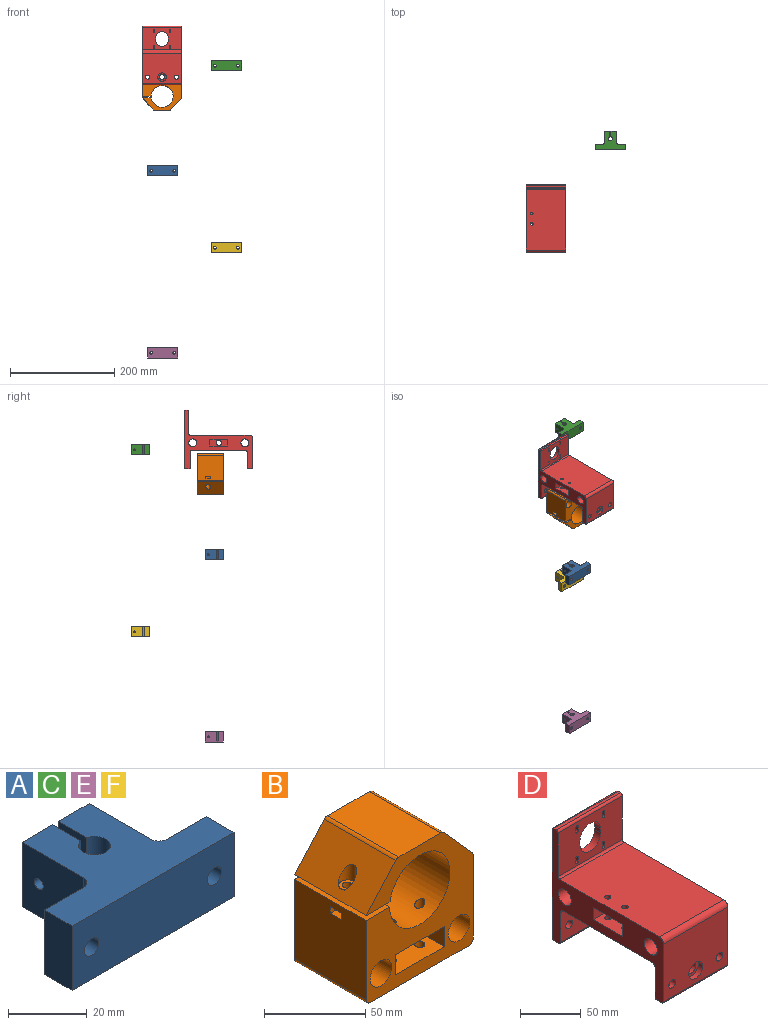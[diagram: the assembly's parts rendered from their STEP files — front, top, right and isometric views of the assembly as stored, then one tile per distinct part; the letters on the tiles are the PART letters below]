
ASSEMBLY  parts=6 mates=3
PART A: 27 faces, bbox 58.1x35x20 mm
  f0: plane 22x20mm, normal (1,0,0), area 413.8mm2, adj f5,f6,f15,f16,f18,f19,f20,f21
  f1: cylinder r=1.6mm len=8.05mm, axis (-1,0,0), area 80.9mm2, adj f7,f24
  f2: plane 58.1x20mm, normal (0,-1,0), area 1119.5mm2, adj f3,f14,f15,f16,f25,f26
  f3: plane 20x10mm, normal (1,0,0), area 200mm2, adj f2,f4,f15,f16
  f4: plane 20x14mm, normal (0,1,0), area 258.8mm2, adj f3,f5,f15,f16,f26
  f5: cylinder r=3mm len=20mm, axis (0,0,-1), area 94.2mm2, adj f0,f4,f15,f16
  f6: plane 20x11.05mm, normal (0,1,0), area 221mm2, adj f0,f7,f15,f16
  f7: plane 20x10.08mm, normal (-1,0,0), area 193.5mm2, adj f1,f6,f8,f15,f16
  f8: cylinder r=4.05mm len=20mm, axis (0,0,-1), area 468.5mm2, adj f7,f9,f15,f16
  f9: plane 20x10.08mm, normal (1,0,0), area 193.5mm2, adj f8,f10,f15,f16,f17
  f10: plane 20x11.05mm, normal (0,1,0), area 221mm2, adj f9,f11,f15,f16
  f11: plane 22x20mm, normal (-1,0,0), area 432mm2, adj f10,f12,f15,f16,f17
  f12: cylinder r=3mm len=20mm, axis (0,0,-1), area 94.2mm2, adj f11,f13,f15,f16
  f13: plane 20x14mm, normal (0,1,0), area 258.8mm2, adj f12,f14,f15,f16,f25
  f14: plane 20x10mm, normal (-1,0,0), area 200mm2, adj f2,f13,f15,f16
  f15: plane 58.1x35mm, normal (0,0,1), area 1115.8mm2, adj f0,f2,f3,f4,f5,f6,f7,f8
  f16: plane 58.1x35mm, normal (0,0,-1), area 1115.8mm2, adj f0,f2,f3,f4,f5,f6,f7,f8
  f17: cylinder r=1.6mm len=11.05mm, axis (-1,0,0), area 111.1mm2, adj f9,f11
  f18: plane 3.18x3mm, normal (0,1,0), area 9.5mm2, adj f0,f19,f23,f24
  f19: plane 3x2.75mm, normal (0,0.5,0.87), area 9.5mm2, adj f0,f18,f20,f24
  f20: plane 3x2.75mm, normal (0,-0.5,0.87), area 9.5mm2, adj f0,f19,f21,f24
  f21: plane 3.18x3mm, normal (0,-1,0), area 9.5mm2, adj f0,f20,f22,f24
  f22: plane 3x2.75mm, normal (0,-0.5,-0.87), area 9.5mm2, adj f0,f21,f23,f24
  f23: plane 3x2.75mm, normal (0,0.5,-0.87), area 9.5mm2, adj f0,f18,f22,f24
  f24: plane 6.35x5.5mm, normal (1,0,0), area 18.2mm2, adj f1,f18,f19,f20,f21,f22,f23
  f25: cylinder r=2.6mm len=10mm, axis (0,-1,0), area 163.4mm2, adj f2,f13
  f26: cylinder r=2.6mm len=10mm, axis (0,-1,0), area 163.4mm2, adj f2,f4
PART B: 40 faces, bbox 75x50x78.1 mm
  f0: plane 50x48mm, normal (-1,0,0), area 2367.6mm2, adj f2,f4,f9,f27,f33,f34,f35,f36
  f1: cylinder r=2.55mm len=5.1mm, axis (0,0,1), area 64.1mm2, adj f9,f33
  f2: plane 78.05x75mm, normal (0,-1,0), area 3115mm2, adj f0,f5,f6,f7,f8,f9,f10,f11
  f3: cylinder r=4.5mm len=29mm, axis (0,1,0), area 820mm2, adj f4,f22
  f4: plane 78.05x75mm, normal (0,1,0), area 3468.6mm2, adj f0,f3,f5,f6,f7,f8,f9,f10
  f5: plane 50x49.86mm, normal (1,0,0), area 2492.8mm2, adj f2,f4,f17,f28
  f6: plane 69x50mm, normal (0,0,-1), area 3409.1mm2, adj f2,f4,f23,f24,f27,f28
  f7: cylinder r=7.55mm len=50mm, axis (0,1,0), area 2371.9mm2, adj f2,f4
  f8: cylinder r=7.55mm len=50mm, axis (0,1,0), area 2371.9mm2, adj f2,f4
  f9: plane 50x16.51mm, normal (0,0,1), area 805mm2, adj f0,f1,f2,f4,f10
  f10: cylinder r=21.05mm len=50mm, axis (0,1,0), area 6416mm2, adj f2,f4,f9,f11,f25,f26
  f11: plane 50x16.72mm, normal (0,0,-1), area 815.7mm2, adj f2,f4,f10,f12,f31
  f12: plane 50x23.05mm, normal (-0.74,0,0.67), area 1452.6mm2, adj f2,f4,f11,f13,f29,f30
  f13: cylinder r=3mm len=50mm, axis (0,1,0), area 126mm2, adj f2,f4,f12,f14
  f14: plane 50x29.32mm, normal (0,0,1), area 1465.8mm2, adj f2,f4,f13,f15
  f15: cylinder r=3mm len=50mm, axis (0,1,0), area 126.4mm2, adj f2,f4,f14,f16
  f16: plane 50x22.19mm, normal (0.75,0,0.67), area 1486.7mm2, adj f2,f4,f15,f17
  f17: cylinder r=3mm len=50mm, axis (0,1,0), area 109.2mm2, adj f2,f4,f5,f16
  f18: plane 34.2x21mm, normal (0,0,-1), area 677.3mm2, adj f2,f19,f21,f22,f25,f26
  f19: plane 21x12.2mm, normal (1,0,0), area 256.2mm2, adj f2,f18,f20,f22
  f20: plane 34.2x21mm, normal (0,0,1), area 677.3mm2, adj f2,f19,f21,f22,f23,f24
  f21: plane 21x12.2mm, normal (-1,0,0), area 256.2mm2, adj f2,f18,f20,f22
  f22: plane 34.2x12.2mm, normal (0,-1,0), area 353.6mm2, adj f3,f18,f19,f20,f21
  f23: cylinder r=2.55mm len=7.9mm, axis (0,0,-1), area 126.6mm2, adj f6,f20
  f24: cylinder r=2.55mm len=7.9mm, axis (0,0,-1), area 126.6mm2, adj f6,f20
  f25: cylinder r=2.55mm len=14mm, axis (0,0,-1), area 200.1mm2, adj f10,f18
  f26: cylinder r=2.55mm len=14mm, axis (0,0,-1), area 200.1mm2, adj f10,f18
  f27: cylinder r=3mm len=50mm, axis (0,-1,0), area 235.6mm2, adj f0,f2,f4,f6
  f28: cylinder r=3mm len=50mm, axis (0,1,0), area 235.6mm2, adj f2,f4,f5,f6
  f29: cylinder r=4.5mm len=10.01mm, axis (0,0,-1), area 139.4mm2, adj f12,f32
  f30: cylinder r=4.5mm len=1.75mm, axis (0,0,-1), area 0.1mm2, adj f12,f32
  f31: cylinder r=2.55mm len=5.1mm, axis (0,0,-1), area 64.1mm2, adj f11,f32
  f32: plane 9x9mm, normal (0,0,1), area 43.2mm2, adj f29,f30,f31
  f33: plane 14.3x8.1mm, normal (0,0,-1), area 95.4mm2, adj f0,f1,f35,f36,f37
  f34: plane 14.3x8.1mm, normal (0,0,1), area 95.4mm2, adj f0,f35,f36,f37,f39
  f35: plane 14.3x4mm, normal (0,-1,0), area 57.2mm2, adj f0,f33,f34,f37
  f36: plane 14.3x4mm, normal (0,1,0), area 57.2mm2, adj f0,f33,f34,f37
  f37: plane 8.1x4mm, normal (-1,0,0), area 32.4mm2, adj f33,f34,f35,f36
  f38: plane 5.1x5.1mm, normal (0,0,1), area 20.4mm2, adj f39
  f39: cylinder r=2.55mm len=5.1mm, axis (0,0,1), area 64.1mm2, adj f34,f38
PART C: same geometry as A
PART D: 66 faces, bbox 75x130x113 mm
  f0: cylinder r=8.1mm len=16.2mm, axis (0,1,0), area 254.5mm2, adj f8,f65
  f1: cylinder r=8.1mm len=16.2mm, axis (0,1,0), area 254.5mm2, adj f2,f63
  f2: plane 109x75mm, normal (0,1,0), area 7242.7mm2, adj f1,f5,f9,f20,f21,f26,f40,f41
  f3: plane 75x44mm, normal (0,-1,0), area 2671.8mm2, adj f5,f9,f39,f41,f42,f43,f44,f45
  f4: plane 116x75mm, normal (0,0,1), area 8659.1mm2, adj f5,f9,f24,f34,f35,f61
  f5: plane 130x113mm, normal (-1,0,0), area 4154.8mm2, adj f2,f3,f4,f7,f8,f10,f11,f12
  f6: cylinder r=5mm len=54mm, axis (-1,0,0), area 1696.5mm2, adj f9,f33
  f7: plane 104x75mm, normal (0,0,-1), area 7759.1mm2, adj f5,f9,f16,f17,f36,f37
  f8: plane 75x58mm, normal (0,-1,0), area 4045.8mm2, adj f0,f5,f9,f18,f19,f24,f27
  f9: plane 130x113mm, normal (1,0,0), area 4493.5mm2, adj f2,f3,f4,f6,f7,f8,f10,f11
  f10: cylinder r=7.55mm len=75mm, axis (-1,0,0), area 3557.9mm2, adj f5,f9
  f11: cylinder r=7.55mm len=75mm, axis (-1,0,0), area 3557.9mm2, adj f5,f9
  f12: plane 75x30mm, normal (0,-1,0), area 2070.3mm2, adj f5,f9,f16,f20,f21,f25,f62
  f13: plane 75x6mm, normal (0,0,-1), area 450mm2, adj f5,f9,f25,f26
  f14: plane 75x30mm, normal (0,1,0), area 2070.3mm2, adj f5,f9,f17,f18,f19,f28,f64
  f15: plane 75x6mm, normal (0,0,-1), area 443.7mm2, adj f5,f9,f22,f23,f27,f28
  f16: cylinder r=3mm len=75mm, axis (1,0,0), area 353.4mm2, adj f5,f7,f9,f12
  f17: cylinder r=3mm len=75mm, axis (-1,0,0), area 353.4mm2, adj f5,f7,f9,f14
  f18: cylinder r=3.95mm len=10mm, axis (0,1,0), area 245mm2, adj f8,f14,f23
  f19: cylinder r=3.95mm len=10mm, axis (0,1,0), area 245mm2, adj f8,f14,f22
  f20: cylinder r=3.95mm len=10mm, axis (0,1,0), area 248.2mm2, adj f2,f12
  f21: cylinder r=3.95mm len=10mm, axis (0,1,0), area 248.2mm2, adj f2,f12
  f22: cylinder r=1mm len=11.18mm, axis (0,0,-1), area 69.8mm2, adj f15,f19
  f23: cylinder r=1mm len=11.18mm, axis (0,0,-1), area 69.8mm2, adj f15,f18
  f24: cylinder r=5mm len=75mm, axis (-1,0,0), area 589mm2, adj f4,f5,f8,f9
  f25: cylinder r=2mm len=75mm, axis (1,0,0), area 235.6mm2, adj f5,f9,f12,f13
  f26: cylinder r=2mm len=75mm, axis (1,0,0), area 235.6mm2, adj f2,f5,f9,f13
  f27: cylinder r=2mm len=75mm, axis (-1,0,0), area 235.6mm2, adj f5,f8,f9,f15
  f28: cylinder r=2mm len=75mm, axis (-1,0,0), area 235.6mm2, adj f5,f9,f14,f15
  f29: plane 21x12.2mm, normal (0,-1,0), area 256.2mm2, adj f5,f30,f32,f33
  f30: plane 34.2x21mm, normal (0,0,1), area 677.3mm2, adj f5,f29,f31,f33,f36,f37
  f31: plane 21x12.2mm, normal (0,1,0), area 256.2mm2, adj f5,f30,f32,f33
  f32: plane 34.2x21mm, normal (0,0,-1), area 677.3mm2, adj f5,f29,f31,f33,f34,f35
  f33: plane 34.2x12.2mm, normal (-1,0,0), area 338.7mm2, adj f6,f29,f30,f31,f32
  f34: cylinder r=2.55mm len=8.9mm, axis (0,0,1), area 142.6mm2, adj f4,f32
  f35: cylinder r=2.55mm len=8.9mm, axis (0,0,1), area 142.6mm2, adj f4,f32
  f36: cylinder r=2.55mm len=8.9mm, axis (0,0,1), area 142.6mm2, adj f7,f30
  f37: cylinder r=2.55mm len=8.9mm, axis (0,0,1), area 142.6mm2, adj f7,f30
  f38: plane 75x3mm, normal (0,0,1), area 225mm2, adj f5,f9,f39,f40
  f39: cylinder r=2mm len=75mm, axis (-1,0,0), area 235.6mm2, adj f3,f5,f9,f38
  f40: cylinder r=2mm len=75mm, axis (1,0,0), area 235.6mm2, adj f2,f5,f9,f38
  f41: cylinder r=12mm len=24mm, axis (0,-1,0), area 263.9mm2, adj f2,f3,f42,f44
  f42: plane 7x4mm, normal (-1,0,0), area 28mm2, adj f2,f3,f41,f43
  f43: cylinder r=12mm len=24mm, axis (0,-1,0), area 263.9mm2, adj f2,f3,f42,f44
  f44: plane 7x4mm, normal (1,0,0), area 28mm2, adj f2,f3,f41,f43
  f45: cylinder r=1.55mm len=7mm, axis (0,-1,0), area 34.1mm2, adj f2,f3,f46,f48
  f46: plane 7x4mm, normal (-1,0,0), area 28mm2, adj f2,f3,f45,f47
  f47: cylinder r=1.55mm len=7mm, axis (0,-1,0), area 34.1mm2, adj f2,f3,f46,f48
  f48: plane 7x4mm, normal (1,0,0), area 28mm2, adj f2,f3,f45,f47
  f49: plane 7x4mm, normal (-1,0,0), area 28mm2, adj f2,f3,f50,f52
  f50: cylinder r=1.55mm len=7mm, axis (0,-1,0), area 34.1mm2, adj f2,f3,f49,f51
  f51: plane 7x4mm, normal (1,0,0), area 28mm2, adj f2,f3,f50,f52
  f52: cylinder r=1.55mm len=7mm, axis (0,-1,0), area 34.1mm2, adj f2,f3,f49,f51
  f53: cylinder r=1.55mm len=7mm, axis (0,-1,0), area 34.1mm2, adj f2,f3,f54,f56
  f54: plane 7x4mm, normal (-1,0,0), area 28mm2, adj f2,f3,f53,f55
  f55: cylinder r=1.55mm len=7mm, axis (0,-1,0), area 34.1mm2, adj f2,f3,f54,f56
  f56: plane 7x4mm, normal (1,0,0), area 28mm2, adj f2,f3,f53,f55
  f57: plane 7x4mm, normal (1,0,0), area 28mm2, adj f2,f3,f58,f60
  f58: cylinder r=1.55mm len=7mm, axis (0,-1,0), area 34.1mm2, adj f2,f3,f57,f59
  f59: plane 7x4mm, normal (-1,0,0), area 28mm2, adj f2,f3,f58,f60
  f60: cylinder r=1.55mm len=7mm, axis (0,-1,0), area 34.1mm2, adj f2,f3,f57,f59
  f61: cylinder r=2mm len=75mm, axis (1,0,0), area 235.6mm2, adj f3,f4,f5,f9
  f62: cylinder r=5.1mm len=10.2mm, axis (0,-1,0), area 160.2mm2, adj f12,f63
  f63: plane 16.2x16.2mm, normal (0,1,0), area 124.4mm2, adj f1,f62
  f64: cylinder r=5.1mm len=10.2mm, axis (0,1,0), area 160.2mm2, adj f14,f65
  f65: plane 16.2x16.2mm, normal (0,-1,0), area 124.4mm2, adj f0,f64
PART E: same geometry as A
PART F: same geometry as A
PLACE A t=(1.32,12.04,-196.34)mm
PLACE B rot(axis=(1,0,0),180deg) t=(-8.34,8.35,7.2)mm
PLACE C t=(123.34,153.59,5.01)mm
PLACE D t=(0,0,13.2)mm
PLACE E t=(1.32,12.04,-545.34)mm
PLACE F t=(123.34,153.59,-343.99)mm
MATE slider A.f8 <-> E.f8  axis (0,0,1) through (1.32,12.04,-176.34)mm
MATE slider F.f8 <-> C.f8  axis (0,0,-1) through (123.34,153.59,-343.99)mm
MATE slider B.f8 <-> D.f18  axis (0,1,0) through (27.5,41.4,-6.8)mm
